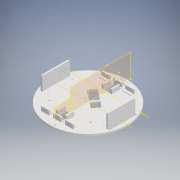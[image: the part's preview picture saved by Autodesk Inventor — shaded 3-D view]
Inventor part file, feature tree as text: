
AUTODESK INVENTOR PART (.ipt)
format: ipt  version: 2020 (Build 240168000, 168)  size: 1,658,880 bytes
history: native  units: mm
features: sketch x42, projected_geometry x35, extrude x30, reference x8, other x7, fillet x5, plane x3, pattern_circular x2, mirror x2
ambient origin geometry x8: Origin, YZ Plane, XZ Plane, XY Plane, X Axis, Y Axis, Z Axis, Center Point
bodies: Solid1 (feature_tree)
feature tree (134):
  other  "Gornja_konstrukcija_s_držačima_assembly.iam"
  other  "GornjaKonstrukcija_lidari_kamere_v.2.0.ipt:1"
  other  "5DržačaLidara.ipt:1"
  other  "5DržačaLidara.ipt:2"
  extrude  "Extrusion1"  Depth=2.0mm TaperAngle=0.0deg
  pattern_circular  "Circular Pattern1"  Count=2 Angle=180.0deg
  extrude  "Extrusion2"  Depth=2.0mm TaperAngle=0.0deg
  extrude  "Extrusion3"  Depth=3.0mm TaperAngle=0.0deg
  sketch  "Sketch15"  dims[d46=3.0mm d47=0.0mm]
  extrude  "Extrusion4"  Depth=3.0mm TaperAngle=0.0deg
  extrude  "Extrusion5"  Depth=3.0mm TaperAngle=360.0deg
  extrude  "Extrusion6"  Depth=3.0mm TaperAngle=0.0deg
  extrude  "Extrusion7"  Depth=3.0mm TaperAngle=0.0deg
  extrude  "Extrusion8"  Depth=10.0mm TaperAngle=0.0deg
  pattern_circular  "Circular Pattern2"  [2 undecoded]
  extrude  "Extrusion9"  [1 undecoded]
  extrude  "Extrusion10"  [1 undecoded]
  extrude  "Extrusion11"  [1 undecoded]
  extrude  "Extrusion12"  [1 undecoded]
  extrude  "Extrusion13"  [1 undecoded]
  extrude  "Extrusion14"  [1 undecoded]
  extrude  "Extrusion15"  [1 undecoded]
  fillet  "Fillet1"  [1 undecoded]
  extrude  "Extrusion16"  [1 undecoded]
  extrude  "Extrusion17"  [1 undecoded]
  extrude  "Extrusion18"  [1 undecoded]
  extrude  "Extrusion19"  [1 undecoded]
  extrude  "Extrusion20"  [1 undecoded]
  extrude  "Extrusion21"  [1 undecoded]
  fillet  "Fillet2"  [1 undecoded]
  extrude  "Extrusion22"  [1 undecoded]
  mirror  "Mirror2"
  extrude  "Extrusion23"  [1 undecoded]
  sketch  "Sketch36"
  extrude  "Extrusion24"  [1 undecoded]
  extrude  "Extrusion25"  [1 undecoded]
  extrude  "Extrusion26"  [1 undecoded]
  mirror  "Mirror3"
  extrude  "Extrusion27"  [1 undecoded]
  sketch  "Sketch41"
  extrude  "Extrusion28"  [1 undecoded]
  fillet  "Fillet4"  [1 undecoded]
  fillet  "Fillet5"  [1 undecoded]
  extrude  "Extrusion29"  [1 undecoded]
  fillet  "Fillet6"  [1 undecoded]
  extrude  "Extrusion31"  [1 undecoded]
  plane  "Work Plane1"
  plane  "Work Plane1_1"
  plane  "Work Plane3"
  other  "Work Axis1"
  sketch  "Sketch8"  dims[d39=2.0mm]
  sketch  "Sketch8_1"  dims[d0=10.0mm d1=2.0mm d2=0.0mm d3=20.0mm d4=180.0deg]
  sketch  "Sketch8_2"  dims[d23=2.0mm d24=0.0mm d25=3.0mm d26=0.0mm]
  sketch  "Sketch8_3"  dims[d27=3.0mm d28=0.0mm d29=3.0mm d30=0.0mm]
  sketch  "Sketch8_4"  dims[d31=10.0mm d32=5.0mm d33=0.0mm d34=0.0mm d35=10.0mm d36=0.0mm]
  sketch  "Sketch8_5"  dims[d37=10.0mm d38=0.0mm]
  sketch  "Sketch8_1_1"  dims[d6=10.0mm d7=0.0mm d8=2.0mm d9=0.0mm]
  sketch  "Sketch8_2_1"  dims[d10=2.0mm d11=0.0mm d12=3.0mm d13=0.0mm]
  sketch  "Sketch8_3_1"  dims[d14=2.0mm d15=0.0mm d16=3.0mm d17=0.0mm]
  sketch  "Sketch8_4_1"  dims[d18=3.0mm d19=0.0mm d20=20.0mm d21=360.0deg]
  sketch  "Sketch12"  dims[d40=3.0mm d41=0.0mm]
  sketch  "Sketch13"  dims[d42=3.0mm d43=0.0mm]
  sketch  "Sketch14"  dims[d44=3.0mm d45=0.0mm]
  projected_geometry  "Projected Loop1"
  projected_geometry  "Projected Loop2"
  projected_geometry  "Projected Loop3"
  projected_geometry  "Projected Loop4"
  sketch  "Sketch16"  dims[d48=3.0mm]
  projected_geometry  "Projected Loop5"
  projected_geometry  "Projected Loop6"
  projected_geometry  "Projected Loop7"
  sketch  "Sketch17"  dims[d49=53.0mm]
  projected_geometry  "Projected Loop8"
  projected_geometry  "Projected Loop9"
  projected_geometry  "Projected Loop10"
  projected_geometry  "Projected Loop11"
  sketch  "Sketch18"  dims[d50=26.0mm d51=0.0mm]
  projected_geometry  "Projected Loop12"
  sketch  "Sketch19"  dims[d52=3.0mm d53=0.0mm]
  projected_geometry  "Projected Loop13"
  sketch  "Sketch20"  dims[d54=2.0mm]
  projected_geometry  "Projected Loop14"
  projected_geometry  "Projected Loop15"
  projected_geometry  "Projected Loop16"
  projected_geometry  "Projected Loop17"
  sketch  "Sketch21"  dims[d55=3.0mm d56=0.0mm]
  projected_geometry  "Projected Loop18"
  sketch  "Sketch22"  dims[d57=3.0mm d58=0.0mm]
  projected_geometry  "Projected Loop19"
  sketch  "Sketch23"  dims[d59=3.0mm d60=0.0mm]
  sketch  "Sketch24"  dims[d61=3.0mm d62=0.0mm]
  projected_geometry  "Projected Loop20"
  projected_geometry  "Projected Loop21"
  sketch  "Sketch25"  dims[d63=3.0mm d64=0.0mm]
  projected_geometry  "Projected Loop22"
  sketch  "Sketch26"  dims[d65=3.0mm d66=0.0mm]
  projected_geometry  "Projected Loop23"
  sketch  "Sketch27"  dims[d67=3.0mm]
  reference  "Reference1"
  reference  "Reference2"
  reference  "Reference3"
  reference  "Reference4"
  sketch  "Sketch28"  dims[d68=3.0mm d69=0.0mm]
  sketch  "Sketch30"  dims[d71=1.0mm]
  projected_geometry  "Projected Loop30"
  projected_geometry  "Projected Loop31"
  sketch  "Sketch31"  dims[d72=1.0mm]
  projected_geometry  "Projected Loop32"
  projected_geometry  "Projected Loop33"
  projected_geometry  "Projected Loop34"
  projected_geometry  "Projected Loop35"
  sketch  "Sketch32"  dims[d73=3.0mm d74=0.0mm]
  sketch  "Sketch33"  dims[d75=1.0mm]
  reference  "Reference5"
  reference  "Reference6"
  reference  "Reference7"
  reference  "Reference8"
  sketch  "Sketch34"  dims[d79=0.3mm]
  sketch  "Sketch35"  dims[d80=3.0mm d81=0.0mm]
  projected_geometry  "Projected Loop36"
  sketch  "Sketch37"
  projected_geometry  "Projected Loop37"
  sketch  "Sketch38"
  projected_geometry  "Projected Loop38"
  sketch  "Sketch39"
  sketch  "Sketch40"
  sketch  "Sketch42"
  sketch  "Sketch43"
  projected_geometry  "Projected Loop39"
  sketch  "Sketch45"
  projected_geometry  "Projected Loop42"
  projected_geometry  "Projected Loop43"
  other  "Assembly_for_print.iam"
  other  "Cam V2.1 v1:1"
note: 29 required parameter values undecoded (feature->parameter linkage not recoverable at this tier; creation-order binding heuristic only, values carry confidence <= 0.55)
